# Revit family: Shower-Slidebar-KOHLER-ACCLIV-K-26789T_1
name_source: partatom
category: Specialty Equipment
units: mm (PartAtom-declared; Revit-internal decimal feet)

## family parameters
Cut with Voids When Loaded = No
Host = Face
OmniClass Number = 23.31.25.00
OmniClass Title = Toilet and Bath Specialties
Part Type = Normal
Room Calculation Point = No
Round Connector Dimension = Use Diameter
Shared = No

## types (4) — shared parameters
ADA Compliant = No
Assembly Code = C1030200
Date Modified = 11/22/2022
Default Elevation = 42"
Description = Sliding shower bracket (with storage tray)
Height = 26 15/16"
Length = 5 5/16"
Manufacturer = Kohler Co.
Master Format 2014 = 10 28 00
Master Format 2014 Name = Toilet, Bath, and Laundry Accessories
Material = Premium Metal Construction
Product Documentation Link = https://files.kohler.com.cn
Product Name = ACCLIV
URL = http://www.kohler.com.cn
WaterSense Certified = No
Width = 9 1/16"

## per-type parameters (varying)
| type | Finish | Model | Product Page URL | Secondary Finish | Type |
| AF-Vibrant French Gold | Kohler-Metal-AF-Vibrant_French_Gold | K-26789T-AF | https://www.kohler.com.cn | Kohler-Plastic-0-White | 1 |
| BL-Matte Black | Kohler-Metal-BL-Matte_Black | K-26789T-BL |  | Kohler-Plastic-7-Black_Black | 2 |
| BN-Vibrant Brushed Nickel | Kohler-Metal-BN-Vibrant_Brushed_Nickel | K-26789T-BN | https://www.kohler.com.cn | Kohler-Plastic-58-Thunder_Grey | 3 |
| CP-Polished Chrome | Kohler-Metal-CP-Polished_Chrome | K-26789T-CP | https://www.kohler.com.cn | Kohler-Plastic-0-White | 4 |

## geometry (parser evidence)
native form markers: Sweep x5
no freeform markers — native parametric forms only
